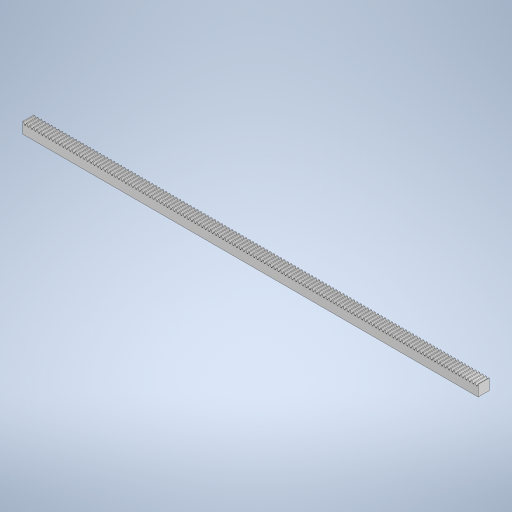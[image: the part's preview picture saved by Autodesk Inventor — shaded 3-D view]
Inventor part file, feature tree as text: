
AUTODESK INVENTOR PART (.ipt)
format: ipt  version: 2023 (Build 270158000, 158)  size: 1,265,152 bytes
history: mixed  units: in
note: dims shown in document units (in); Inventor stores cm internally (conversion verified against a paired STEP export)
features: extrude x1, sketch x1, other x1, imported_body x1
ambient origin geometry x8: Origin, YZ Plane, XZ Plane, XY Plane, X Axis, Y Axis, Z Axis, Center Point
bodies: Solid1 (imported_parasolid)
feature tree (4):
  extrude  "Extrusion1"  Depth=0.3937in
  sketch  "Sketch1"  dims[d0=0.0332in d1=0.0864in d2=0.0082in d3=0.0159in d4=0.0082in d6=0.0082in d7=0.0082in d8=0.0159in d9=0.0082in d10=0.0905in d11=0.7734in d12=0.7734in d117=4.2126in d391=0.0in d392=0.0332in d393=0.0864in d394=0.0082in d395=0.0159in d396=0.0082in d397=0.0082in d398=0.0082in d399=0.0159in d400=0.0082in d401=0.0905in d402=0.7734in d403=0.7734in d404=0.0in d405=0.0332in d406=0.0864in d407=0.0082in d408=0.0159in d409=0.0082in d410=0.0082in d411=0.0082in d412=0.0159in d413=0.0082in d414=0.0905in d415=0.7734in d416=0.7734in d417=0.0in d418=0.0332in d419=0.0864in d420=0.0082in d421=0.0159in d422=0.0082in d423=0.0082in d424=0.0082in d425=0.0159in d426=0.0082in d427=0.0905in d428=0.7734in d429=0.7734in d430=0.0in d431=0.0332in d432=0.0864in d433=0.0082in d434=0.0159in d435=0.0082in d436=0.0082in d437=0.0082in d438=0.0159in d439=0.0082in d440=0.0905in d441=0.7734in d442=0.7734in d443=0.0in d444=0.0332in d445=0.0864in d446=0.0082in d447=0.0159in d448=0.0082in d449=0.0082in d450=0.0082in d451=0.0159in d452=0.0082in d453=0.0905in d454=0.7734in d455=0.7734in d456=0.0in d457=0.0332in d458=0.0864in d459=0.0082in d460=0.0159in d461=0.0082in d462=0.0082in d463=0.0082in d464=0.0159in d465=0.0082in d466=0.0905in d467=0.7734in d468=0.7734in d469=0.0in d470=0.0332in d471=0.0864in d472=0.0082in d473=0.0159in d474=0.0082in d475=0.0082in d476=0.0082in d477=0.0159in d478=0.0082in d479=0.0905in d480=0.7734in d481=0.7734in d482=0.0in d483=0.0332in d484=0.0864in d485=0.0082in d486=0.0159in d487=0.0082in d488=0.0082in d489=0.0082in d490=0.0159in d491=0.0082in d492=0.0905in d493=0.7734in d494=0.7734in d495=0.0in d496=0.0332in d497=0.0864in d498=0.0082in d499=0.0159in d500=0.0082in d501=0.0082in d502=0.0082in d503=0.0159in d504=0.0082in d505=0.0905in d506=0.7734in d507=0.7734in d508=0.0in d509=0.0332in d510=0.0864in d511=0.0082in d512=0.0159in d513=0.0082in d514=0.0082in d515=0.0082in d516=0.0159in d517=0.0082in d518=0.0905in d519=0.7734in d520=0.7734in d521=0.0in d522=0.0332in d523=0.0864in d524=0.0082in d525=0.0159in d526=0.0082in d527=0.0082in d528=0.0082in d529=0.0159in d530=0.0082in d531=0.0905in d532=0.7734in d533=0.7734in d534=0.0in d535=0.0332in d536=0.0864in d537=0.0082in d538=0.0159in d539=0.0082in d540=0.0082in d541=0.0082in d542=0.0159in d543=0.0082in d544=0.0905in d545=0.7734in d546=0.7734in d547=0.0in d548=0.0332in d549=0.0864in d550=0.0082in d551=0.0159in d552=0.0082in d553=0.0082in d554=0.0082in d555=0.0159in d556=0.0082in d557=0.0905in d558=0.7734in d559=0.7734in d560=0.0in d561=0.0332in d562=0.0864in d563=0.0082in d564=0.0159in d565=0.0082in d566=0.0082in d567=0.0082in d568=0.0159in d569=0.0082in d570=0.0905in d571=0.7734in d572=0.7734in d573=0.0in d574=0.0332in d575=0.0864in d576=0.0082in d577=0.0159in d578=0.0082in d579=0.0082in d580=0.0082in d581=0.0159in d582=0.0082in d583=0.0905in d584=0.7734in d585=0.7734in d586=0.0in d587=0.0332in d588=0.0864in d589=0.0082in d590=0.0159in d591=0.0082in d592=0.0082in d593=0.0082in d594=0.0159in d595=0.0082in d596=0.0905in d597=0.7734in d598=0.7734in d599=0.0in d600=0.0332in d601=0.0864in d602=0.0082in d603=0.0159in d604=0.0082in d605=0.0082in d606=0.0082in d607=0.0159in d608=0.0082in d609=0.0905in d610=0.7734in d611=0.7734in d612=0.0in d613=0.0332in d614=0.0864in d615=0.0082in d616=0.0159in d617=0.0082in d618=0.0082in d619=0.0082in d620=0.0159in d621=0.0082in d622=0.0905in d623=0.7734in d624=0.7734in d625=0.0in d626=0.0332in d627=0.0864in d628=0.0082in d629=0.0159in d630=0.0082in d631=0.0082in d632=0.0082in d633=0.0159in d634=0.0082in d635=0.0905in d636=0.7734in d637=0.7734in d638=0.0in d639=0.0332in d640=0.0864in d641=0.0082in d642=0.0159in d643=0.0082in d644=0.0082in d645=0.0082in d646=0.0159in d647=0.0082in d648=0.0905in d649=0.7734in d650=0.7734in d651=0.0in d652=0.0332in d653=0.0864in d654=0.0082in d655=0.0159in d656=0.0082in d657=0.0082in d658=0.0082in d659=0.0159in d660=0.0082in d661=0.0905in d662=0.7734in d663=0.7734in d664=0.0in d665=0.0332in d666=0.0864in d667=0.0082in d668=0.0159in d669=0.0082in d670=0.0082in d671=0.0082in d672=0.0159in d673=0.0082in d674=0.0905in d675=0.7734in d676=0.7734in d677=0.0in d678=0.0332in d679=0.0864in d680=0.0082in d681=0.0159in d682=0.0082in d683=0.0082in d684=0.0082in d685=0.0159in d686=0.0082in d687=0.0905in d688=0.7734in d689=0.7734in d690=0.0in d691=0.0332in d692=0.0864in d693=0.0082in d694=0.0159in d695=0.0082in d696=0.0082in d697=0.0082in d698=0.0159in d699=0.0082in d700=0.0905in d701=0.7734in d702=0.7734in d703=0.0in d704=0.0332in d705=0.0864in d706=0.0082in d707=0.0159in d708=0.0082in d709=0.0082in d710=0.0082in d711=0.0159in d712=0.0082in d713=0.0905in d714=0.7734in d715=0.7734in d716=0.0in d717=0.0332in d718=0.0864in d719=0.0082in d720=0.0159in d721=0.0082in d722=0.0082in d723=0.0082in d724=0.0159in d725=0.0082in d726=0.0905in d727=0.7734in d728=0.7734in d729=0.0in d730=0.0332in d731=0.0864in d732=0.0082in d733=0.0159in d734=0.0082in d735=0.0082in d736=0.0082in d737=0.0159in d738=0.0082in d739=0.0905in d740=0.7734in d741=0.7734in d742=0.0in d743=0.0332in d744=0.0864in d745=0.0082in d746=0.0159in d747=0.0082in d748=0.0082in d749=0.0082in d750=0.0159in d751=0.0082in d752=0.0905in d753=0.7734in d754=0.7734in d755=0.0in d756=0.0332in d757=0.0864in d758=0.0082in d759=0.0159in d760=0.0082in d761=0.0082in d762=0.0082in d763=0.0159in d764=0.0082in d765=0.0905in d766=0.7734in d767=0.7734in d768=0.0in d769=0.0332in d770=0.0864in d771=0.0082in d772=0.0159in d773=0.0082in d774=0.0082in d775=0.0082in d776=0.0159in d777=0.0082in d778=0.0905in d779=0.7734in d780=0.7734in d781=0.0in d782=0.0332in d783=0.0864in d784=0.0082in d785=0.0159in d786=0.0082in d787=0.0082in d788=0.0082in d789=0.0159in d790=0.0082in d791=0.0905in d792=0.7734in d793=0.7734in d794=0.0in d795=0.0332in d796=0.0864in d797=0.0082in d798=0.0159in d799=0.0082in d800=0.0082in d801=0.0082in d802=0.0159in d803=0.0082in d804=0.0905in d805=0.7734in d806=0.7734in d807=0.0in d808=0.0332in d809=0.0864in d810=0.0082in d811=0.0159in d812=0.0082in d813=0.0082in d814=0.0082in d815=0.0159in d816=0.0082in d817=0.0905in d818=0.7734in d819=0.7734in d820=0.0in d847=0.3937in d848=0.0in]
  other  "LPattern1"
  imported_body  NMx_Import_Brep_tag  [imported B-rep: ~792 faces, bbox_mm=[411.8, 10.0, 10.0]]
